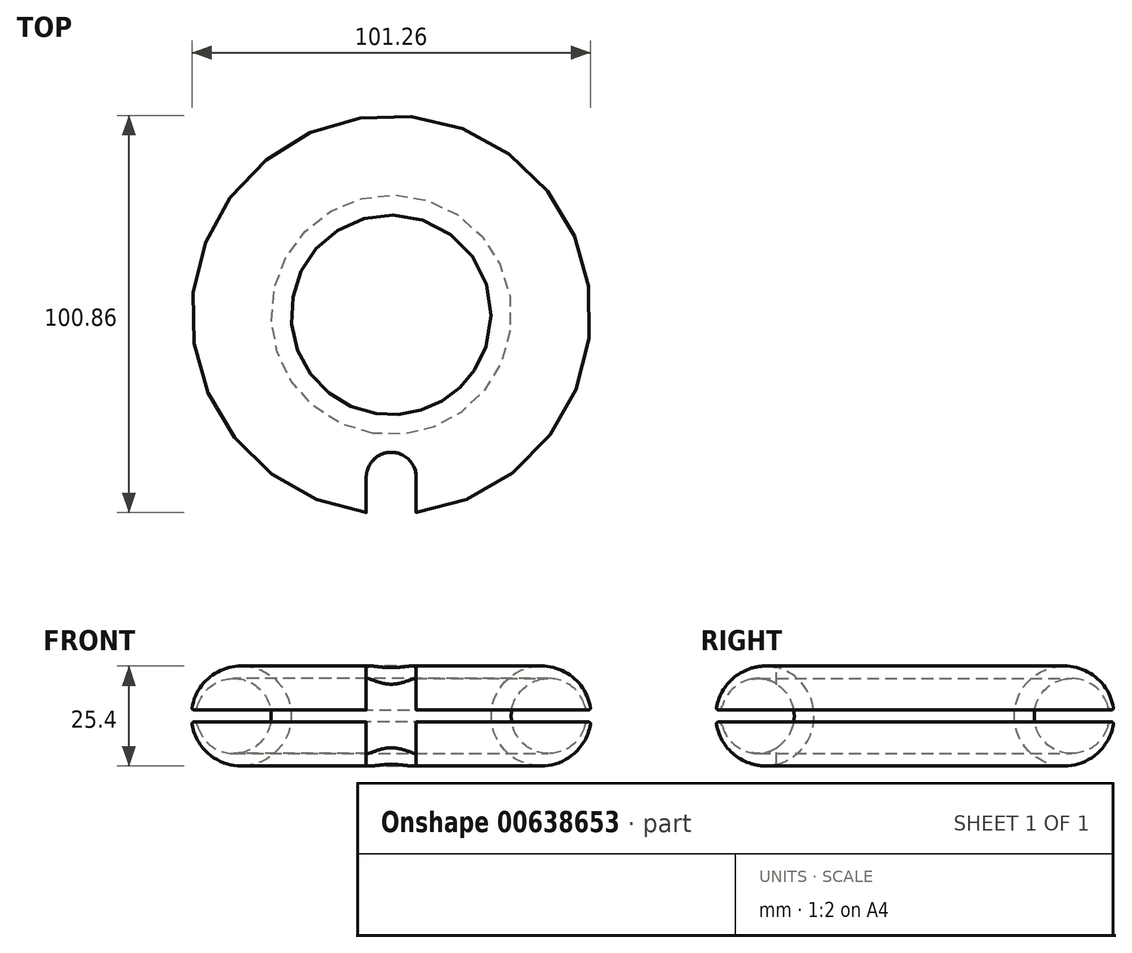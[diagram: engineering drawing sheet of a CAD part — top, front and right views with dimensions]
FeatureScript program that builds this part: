
annotation { "Feature Type Name" : "Feature", "Feature Type Description" : "" }
export const myFeature = defineFeature(function(context is Context, id is Id, definition is map)
    precondition{}
    {
        {
            var Q0;
            Q0=qCreatedBy(makeId("Front.planeOp"),FACE);
            var sketch = newSketch(context, id + "F0", { "sketchPlane" : qUnion([Q0])});
            skArc(sketch, "E0", {"start": v(50.74, 1.27) * mm, "mid": v(25.4, 0) * mm, "end": v(50.74, -1.27) * mm});
            skArc(sketch, "E1", {"start": v(49.44, 1.27) * mm, "mid": v(30.48, 0) * mm, "end": v(49.44, -1.27) * mm});
            skLineSegment(sketch, "E2", {"start": v(49.44, 1.27) * mm, "end": v(50.74, 1.27) * mm});
            skLineSegment(sketch, "E3", {"start": v(49.44, -1.27) * mm, "end": v(50.74, -1.27) * mm});
            skSolve(sketch);
        }
        {
            var Q0;
            Q0=qCreatedBy(makeId("Front.planeOp"),FACE);
            var sketch = newSketch(context, id + "F1", { "sketchPlane" : qUnion([Q0])});
            skLineSegment(sketch, "E4", {"start": v(0, 0) * mm, "end": v(0, 25.4) * mm, "construction": true});
            skSolve(sketch);
        }
        {
            var Q0;
            Q0=makeQuery(id+"F0.imprint","IMPRINT",FACE,{"disambiguationData":[TD([[makeQuery(id+"F0.imprint","IMPRINT",EDGE,{"derivedFrom":sQuery(id+"F0.wireOp",EDGE,"E0")}),1.0]])]});
            var Q1;
            Q1=sQuery(id+"F1.wireOp",EDGE,"E4");
            revolve(context, id + "F2", {"entities" : qUnion([Q0]), "axis" : qUnion([Q1]), "revolveType" : RevolveType.FULL});
        }
        {
            var Q0;
            Q0=makeQuery(id+"F2.opRevolve","SWEPT_EDGE",EDGE,{"disambiguationData":[OSD([sQuery(id+"F0.wireOp",EDGE,"E1"),sQuery(id+"F0.wireOp",EDGE,"E3")])]});
            var Q1;
            Q1=makeQuery(id+"F2.opRevolve","SWEPT_EDGE",EDGE,{"disambiguationData":[OSD([sQuery(id+"F0.wireOp",EDGE,"E1"),sQuery(id+"F0.wireOp",EDGE,"E2")])]});
            fillet(context, id + "F3", {"entities" : qUnion([Q0, Q1]), "radius" : 1.78 * mm, "tangentPropagation" : true, "allowEdgeOverflow" : false});
        }
        {
            var Q0;
            Q0=makeQuery(id+"F3.opFillet","BLEND_EDGE",EDGE,{"blendedFrom":[makeQuery(id+"F2.opRevolve","SWEPT_EDGE",EDGE,{"disambiguationData":[OSD([sQuery(id+"F0.wireOp",EDGE,"E1"),sQuery(id+"F0.wireOp",EDGE,"E3")])]}),makeQuery(id+"F2.opRevolve","SWEPT_FACE",FACE,{"disambiguationData":[OSD([sQuery(id+"F0.wireOp",EDGE,"E0")])]})],"blendedInto":[makeQuery(id+"F2.opRevolve","SWEPT_FACE",FACE,{"disambiguationData":[OSD([sQuery(id+"F0.wireOp",EDGE,"E0")])]})]});
            var Q1;
            Q1=makeQuery(id+"F3.opFillet","BLEND_EDGE",EDGE,{"blendedFrom":[makeQuery(id+"F2.opRevolve","SWEPT_EDGE",EDGE,{"disambiguationData":[OSD([sQuery(id+"F0.wireOp",EDGE,"E1"),sQuery(id+"F0.wireOp",EDGE,"E2")])]}),makeQuery(id+"F2.opRevolve","SWEPT_FACE",FACE,{"disambiguationData":[OSD([sQuery(id+"F0.wireOp",EDGE,"E0")])]})],"blendedInto":[makeQuery(id+"F2.opRevolve","SWEPT_FACE",FACE,{"disambiguationData":[OSD([sQuery(id+"F0.wireOp",EDGE,"E0")])]})]});
            fillet(context, id + "F4", {"entities" : qUnion([Q0, Q1]), "radius" : 0.5 * mm, "allowEdgeOverflow" : false});
        }
        {
            var Q0;
            Q0=qCreatedBy(makeId("Top.planeOp"),FACE);
            cPlane(context, id + "F5", {"entities" : qUnion([Q0]), "cplaneType" : CPlaneType.OFFSET, "offset" : 25.4 * mm, "width" : 152.4 * mm, "height" : 152.4 * mm});
        }
        {
            var Q0;
            Q0=qCreatedBy(id+"F5.planeOp",FACE);
            var sketch = newSketch(context, id + "F6", { "sketchPlane" : qUnion([Q0])});
            skArc(sketch, "E5", {"start": v(-6.35, -34.34) * mm, "mid": v(0, -34.93) * mm, "end": v(6.35, -34.34) * mm});
            skLineSegment(sketch, "E6", {"start": v(-6.35, -34.34) * mm, "end": v(-6.35, -58.81) * mm});
            skLineSegment(sketch, "E7", {"start": v(6.35, -34.34) * mm, "end": v(6.35, -58.81) * mm});
            skLineSegment(sketch, "E8", {"start": v(-6.35, -58.81) * mm, "end": v(6.35, -58.81) * mm});
            skSolve(sketch);
        }
        {
            var Q0;
            Q0=makeQuery(id+"F6.imprint","IMPRINT",FACE,{"disambiguationData":[TD([[makeQuery(id+"F6.imprint","IMPRINT",EDGE,{"derivedFrom":sQuery(id+"F6.wireOp",EDGE,"E5")}),-1.0]])]});
            extrude(context, id + "F7", {"entities" : qUnion([Q0]), "operationType" : NewBodyOperationType.REMOVE, "oppositeDirection" : true, "depth" : 49.18 * mm, "offsetDistance" : 25.4 * mm});
        }
        {
            var Q0;
            Q0=makeQuery(id+"F7.boolean.opBoolean","COPY",EDGE,{"disambiguationData":[OD(0.0)],"derivedFrom":makeQuery(id+"F7.opExtrude","SWEPT_EDGE",EDGE,{"disambiguationData":[OSD([sQuery(id+"F6.wireOp",EDGE,"E5"),sQuery(id+"F6.wireOp",EDGE,"E7")])]})});
            var Q1;
            Q1=makeQuery(id+"F7.boolean.opBoolean","COPY",EDGE,{"disambiguationData":[OD(0.0)],"derivedFrom":makeQuery(id+"F7.opExtrude","SWEPT_EDGE",EDGE,{"disambiguationData":[OSD([sQuery(id+"F6.wireOp",EDGE,"E5"),sQuery(id+"F6.wireOp",EDGE,"E6")])]})});
            var Q2;
            Q2=makeQuery(id+"F7.boolean.opBoolean","COPY",EDGE,{"disambiguationData":[OD(1.0)],"derivedFrom":makeQuery(id+"F7.opExtrude","SWEPT_EDGE",EDGE,{"disambiguationData":[OSD([sQuery(id+"F6.wireOp",EDGE,"E5"),sQuery(id+"F6.wireOp",EDGE,"E6")])]})});
            var Q3;
            Q3=makeQuery(id+"F7.boolean.opBoolean","COPY",EDGE,{"disambiguationData":[OD(1.0)],"derivedFrom":makeQuery(id+"F7.opExtrude","SWEPT_EDGE",EDGE,{"disambiguationData":[OSD([sQuery(id+"F6.wireOp",EDGE,"E5"),sQuery(id+"F6.wireOp",EDGE,"E7")])]})});
            fillet(context, id + "F8", {"entities" : qUnion([Q0, Q1, Q2, Q3]), "radius" : 6.35 * mm, "tangentPropagation" : true, "allowEdgeOverflow" : false});
        }
    });
